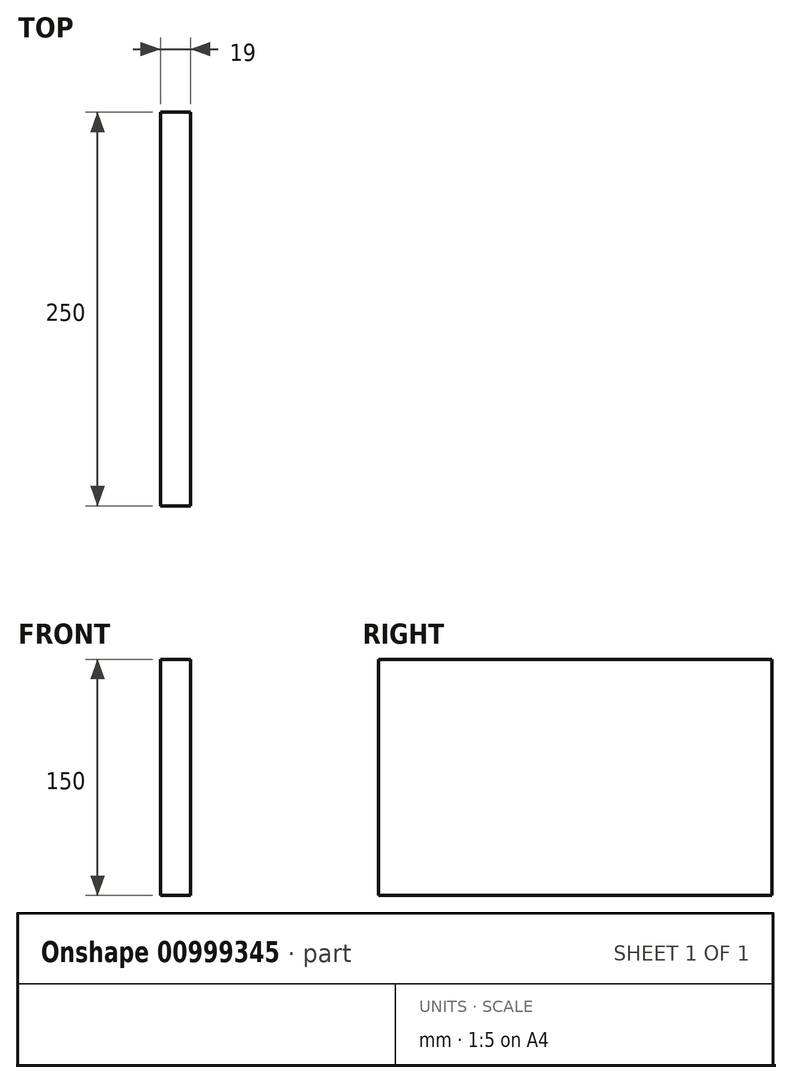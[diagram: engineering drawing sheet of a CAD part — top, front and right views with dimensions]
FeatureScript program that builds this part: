
annotation { "Feature Type Name" : "Feature", "Feature Type Description" : "" }
export const myFeature = defineFeature(function(context is Context, id is Id, definition is map)
    precondition{}
    {
        {
            var Q0;
            Q0=qCreatedBy(makeId("Right.planeOp"),FACE);
            var sketch = newSketch(context, id + "F0", { "sketchPlane" : qUnion([Q0])});
            skLineSegment(sketch, "E0.bottom", {"start": v(0, 0) * mm, "end": v(250, 0) * mm});
            skLineSegment(sketch, "E0.top", {"start": v(0, 150) * mm, "end": v(250, 150) * mm});
            skLineSegment(sketch, "E0.left", {"start": v(0, 0) * mm, "end": v(0, 150) * mm});
            skLineSegment(sketch, "E0.right", {"start": v(250, 0) * mm, "end": v(250, 150) * mm});
            skSolve(sketch);
        }
        {
            var Q0;
            Q0 = qSketchRegion(id + "F0", true);
            extrude(context, id + "F1", {"entities" : qUnion([Q0]), "oppositeDirection" : true, "depth" : 19 * mm, "offsetDistance" : 25 * mm});
        }
    });
